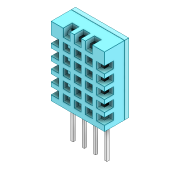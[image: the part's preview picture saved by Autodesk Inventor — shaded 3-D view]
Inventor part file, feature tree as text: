
AUTODESK INVENTOR PART (.ipt)
format: ipt  version: 2021 (Build 250183000, 183)  size: 422,912 bytes
history: native  units: mm
features: other x10, fillet x2
ambient origin geometry x8: Origin, YZ Plane, XZ Plane, XY Plane, X Axis, Y Axis, Z Axis, Center Point
bodies: Body1 (feature_tree), Body2 (feature_tree), Body3 (feature_tree), Body4 (feature_tree), Body5 (feature_tree), Body6 (feature_tree)
feature tree (12):
  other  "Твердое тело1"
  other  "Твердое тело2"
  other  "Твердое тело3"
  other  "Твердое тело4"
  other  "Твердое тело5"
  other  "Твердое тело6"
  fillet  "Fillet1"  [1 undecoded]
  other  "Cut-Extrude5[2]"
  other  "Cut-Extrude5[3]"
  other  "Cut-Extrude5[4]"
  other  "Cut-Extrude5[5]"
  fillet  "Fillet3"  [1 undecoded]
note: 2 required parameter values undecoded (feature->parameter linkage not recoverable at this tier; creation-order binding heuristic only, values carry confidence <= 0.55)
